# Revit family: HL_RU_Floor drain_HL5100-A-160411
name_source: partatom
category: Instalační zařizovací předměty
units: mm (PartAtom-declared; Revit-internal decimal feet)

## family parameters
Bod výpočtu místnosti = Ano
Kóta kulaté spojky = Použít průměr
Nadpis OmniClass = Deck Waste Water Drains
Ořezat dutým tvarem při načtení = Ne
Sdílené = Ano
Typ dílu = Normální
Vždy vertikální = Ano
Založené na pracovní rovině = Ne
Číslo OmniClass = 23.70.50.21.24.14

## types (1)
- HL5100
    EAN = 9003076025442
    Indexovaná poznámka = HL5100
    Komentáře k typům = HL5100 Трап для внутренних помещений DN50/75 горизонтальный 145x145 мм система крепления решётки Klick-Klack/138x138мм
    Model = HL5100
    Popis = Трапы для внутренних помещений
    Přípoj CW = Ne
    Přípoj HW = Ne
    Přípoj odpadních dílů = Ano
    Přípoj ventilace = Ne
    URL = http://www.hutterer-lechner.com
    Výchozí výška = 0 mm  [stored 0 ft]
    Výrobce = HL Hutterer & Lechner GmbH
    ВЕС = 1,03 [kg]
    ВЫСОТА МОНТАЖА = 105 mm
    МАКСИМАЛЬНАЯ НАГРУЗКА КЛАССА = K3 - 300kg
    МАТЕРИАЛ = PE
    НАСАДКА = 8-80 mm / 145 x 145 mm / PP-V4A
    НОМИНАЛЬНЫЙ ДИАМЕТР = 75 mm
    ПРОИЗВОДИТЕЛЬНОСТЬ = 1,0 l/s
    ПРОПУСКНАЯ СПОСОБНОСТЬ = 1.0 L/s
    РАЗМЕР = DN50/75
    РЕШЁТКА = 138 x 138 mm / V2A

note: [stored X ft] marks values corroborated as IEEE doubles in the binary element streams (Revit-internal decimal feet)

## geometry (parser evidence)
native form markers: Sweep x39
no freeform markers — native parametric forms only
